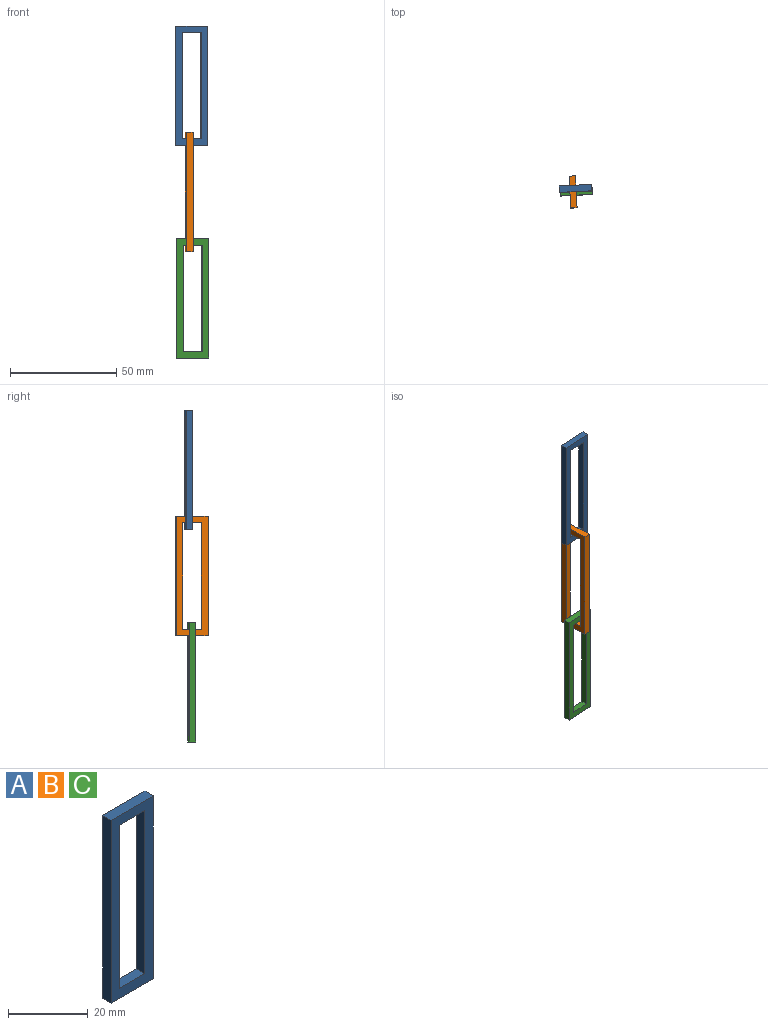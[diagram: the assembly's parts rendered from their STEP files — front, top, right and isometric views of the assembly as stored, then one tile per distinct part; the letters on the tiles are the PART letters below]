
ASSEMBLY  parts=3 mates=3
PART A: 10 faces, bbox 15x3x56 mm
  f0: plane 15x3mm, normal (0,0,1), area 45mm2, adj f1,f7,f8,f9
  f1: plane 56x3mm, normal (-1,0,0), area 168mm2, adj f0,f2,f8,f9
  f2: plane 15x3mm, normal (0,0,-1), area 45mm2, adj f1,f7,f8,f9
  f3: plane 50x3mm, normal (1,0,0), area 150mm2, adj f4,f6,f8,f9
  f4: plane 9x3mm, normal (0,0,-1), area 27mm2, adj f3,f5,f8,f9
  f5: plane 50x3mm, normal (-1,0,0), area 150mm2, adj f4,f6,f8,f9
  f6: plane 9x3mm, normal (0,0,1), area 27mm2, adj f3,f5,f8,f9
  f7: plane 56x3mm, normal (1,0,0), area 168mm2, adj f0,f2,f8,f9
  f8: plane 56x15mm, normal (0,-1,0), area 390mm2, adj f0,f1,f2,f3,f4,f5,f6,f7
  f9: plane 56x15mm, normal (0,1,0), area 390mm2, adj f0,f1,f2,f3,f4,f5,f6,f7
PART B: same geometry as A
PART C: same geometry as A
PLACE A rot(axis=(0,0,1),2.8deg) t=(3.98,1.68,72.5)mm
PLACE B rot(axis=(0,0,1),92.8deg) t=(1.43,-1.44,22.5)mm
PLACE C rot(axis=(0,0,1),2.8deg) t=(4.45,0.2,-27.5)mm
MATE planar C.f4 <-> B.f6  axis (0,0,-1) through (4.53,-1.29,-2.5)mm
MATE planar A.f6 <-> B.f4  axis (0,0,1) through (4.13,-1.31,47.5)mm
MATE parallel B.f8 <-> C.f7  axis (1,0.05,0) through (4.43,-1.3,22.5)mm
